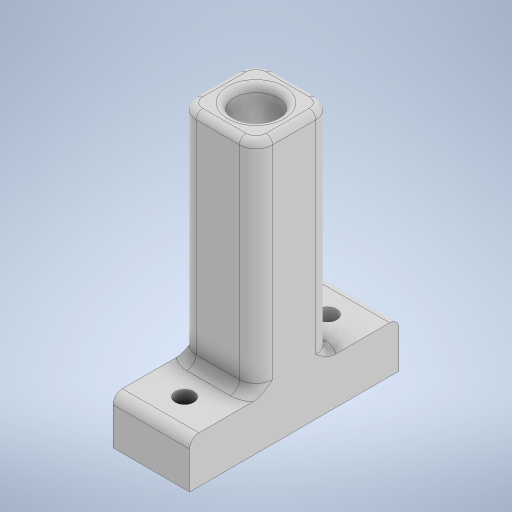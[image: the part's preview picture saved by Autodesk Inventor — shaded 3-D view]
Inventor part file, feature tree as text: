
AUTODESK INVENTOR PART (.ipt)
format: ipt  version: 2024.2 (Build 282272000, 272)  size: 674,304 bytes
history: native  units: in
note: dims shown in document units (in); Inventor stores cm internally (conversion verified against a paired STEP export)
features: fillet x5, extrude x3, sketch x1
ambient origin geometry x8: Origin, YZ Plane, XZ Plane, XY Plane, X Axis, Y Axis, Z Axis, Center Point
bodies: Solid1 (feature_tree)
feature tree (9):
  sketch  "Sketch1"  dims[d0=0.325in d1=0.2875in d2=0.288in d3=0.288in d4=0.288in d5=0.14in d6=0.14in d7=0.5in d8=0.5in d9=0.25in d10=0.25in d11=0.35in d12=0.0in d16=2.0in d17=0.0in d18=0.125in d20=0.05in d21=1.25in d22=0.0in d23=0.5in d24=0.5in d25=0.156in d26=0.156in d28=0.07in d29=0.07in d30=0.05in]
  extrude  "Extrusion1"  Depth=0.05in
  extrude  "Extrusion2"  Depth=0.05in
  fillet  "Fillet1"  Radius=0.288in
  fillet  "Fillet3"  Radius=0.288in
  extrude  "Extrusion3"  Depth=0.05in
  fillet  "Fillet5"  Radius=0.14in
  fillet  "Fillet6"  Radius=0.5in
  fillet  "Fillet7"  Radius=0.5in
